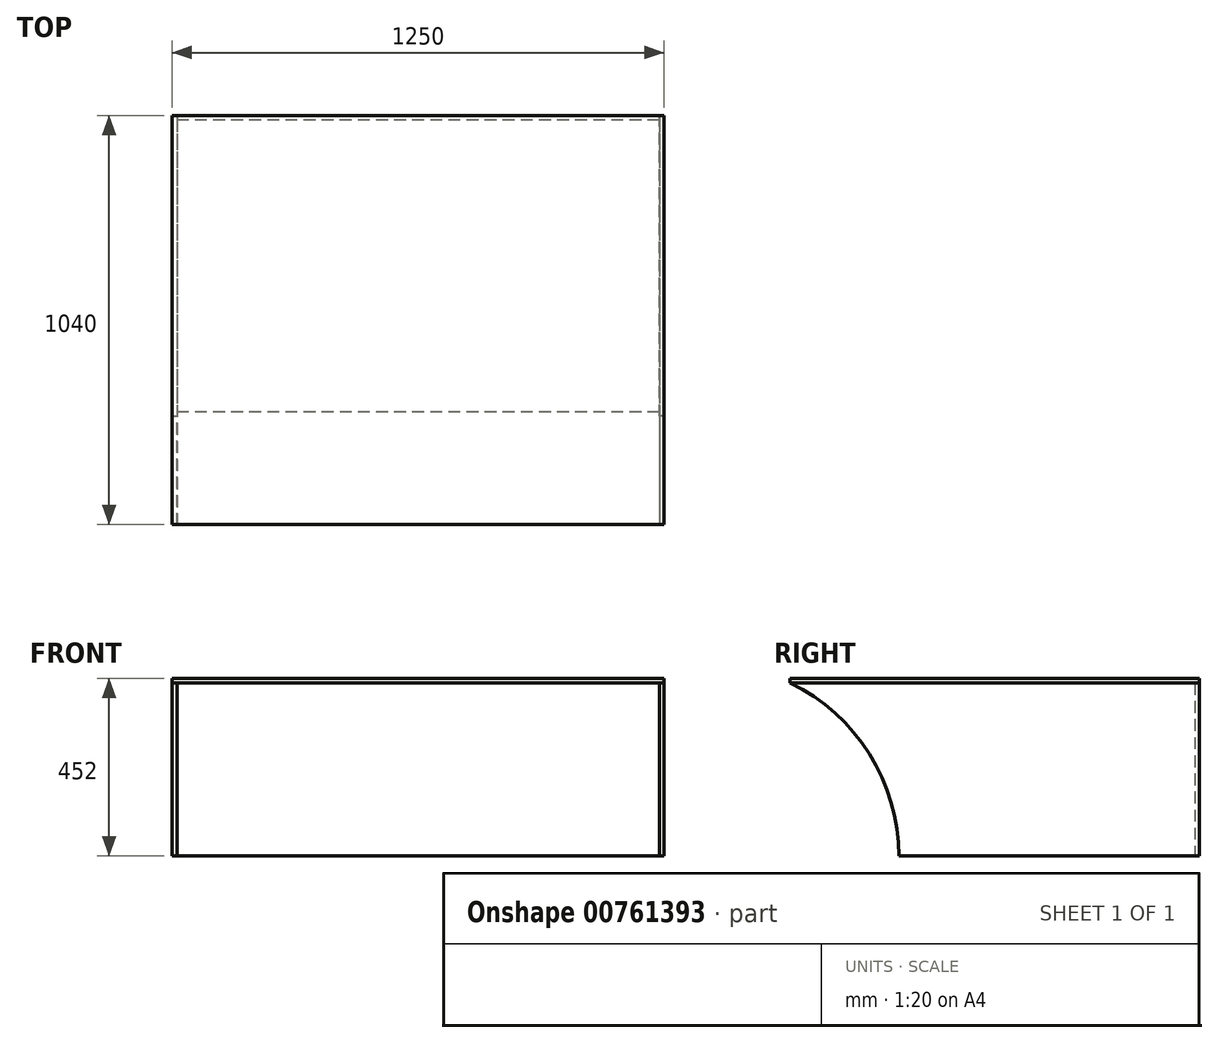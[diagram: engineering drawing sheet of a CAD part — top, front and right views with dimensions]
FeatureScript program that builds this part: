
annotation { "Feature Type Name" : "Feature", "Feature Type Description" : "" }
export const myFeature = defineFeature(function(context is Context, id is Id, definition is map)
    precondition{}
    {
        {
            var Q0;
            Q0=qCreatedBy(makeId("Top.planeOp"),FACE);
            var sketch = newSketch(context, id + "F0", { "sketchPlane" : qUnion([Q0])});
            skLineSegment(sketch, "E0.bottom", {"start": v(-622.3, 286.42) * mm, "end": v(603.7, 286.42) * mm});
            skLineSegment(sketch, "E0.top", {"start": v(-622.3, -453.58) * mm, "end": v(603.7, -453.58) * mm});
            skLineSegment(sketch, "E0.left", {"start": v(-622.3, 286.42) * mm, "end": v(-622.3, -453.58) * mm});
            skLineSegment(sketch, "E0.right", {"start": v(603.7, 286.42) * mm, "end": v(603.7, -453.58) * mm});
            skSolve(sketch);
        }
        {
            var Q0;
            Q0=makeQuery(id+"F0.imprint","IMPRINT",FACE,{"disambiguationData":[TD([[makeQuery(id+"F0.imprint","IMPRINT",EDGE,{"derivedFrom":sQuery(id+"F0.wireOp",EDGE,"E0.bottom")}),-1.0]])]});
            extrude(context, id + "F1", {"entities" : qUnion([Q0]), "depth" : 1 * mm, "offsetDistance" : 25 * mm});
        }
        {
            var Q0;
            Q0=makeQuery(id+"F1.opExtrude","SWEPT_FACE",FACE,{"disambiguationData":[OSD([sQuery(id+"F0.wireOp",EDGE,"E0.bottom")])]});
            var sketch = newSketch(context, id + "F2", { "sketchPlane" : qUnion([Q0])});
            skLineSegment(sketch, "E1.bottom", {"start": v(-603.7, 440) * mm, "end": v(622.3, 440) * mm});
            skLineSegment(sketch, "E1.top", {"start": v(-603.7, 0) * mm, "end": v(622.3, 0) * mm});
            skLineSegment(sketch, "E1.left", {"start": v(-603.7, 440) * mm, "end": v(-603.7, 0) * mm});
            skLineSegment(sketch, "E1.right", {"start": v(622.3, 440) * mm, "end": v(622.3, 0) * mm});
            skSolve(sketch);
        }
        {
            var Q0;
            {var subQ0=sQuery(id+"F2.wireOp",EDGE,"E1.bottom");Q0=makeQuery(id+"F2.imprint","IMPRINT",FACE,{"disambiguationData":[TD([[makeQuery(id+"F2.imprint","IMPRINT",EDGE,{"derivedFrom":subQ0}),-1.0]])]});}
            var Q1;
            {var subQ0=sQuery(id+"F2.wireOp",EDGE,"E1.top");Q1=makeQuery(id+"F2.imprint","IMPRINT",FACE,{"disambiguationData":[TD([[makeQuery(id+"F2.imprint","IMPRINT",EDGE,{"derivedFrom":subQ0}),-1.0]])]});}
            extrude(context, id + "F3", {"entities" : qUnion([Q0, Q1]), "depth" : 12 * mm, "offsetDistance" : 25 * mm});
        }
        {
            var Q0;
            Q0=makeQuery(id+"F1.opExtrude","SWEPT_FACE",FACE,{"disambiguationData":[OSD([sQuery(id+"F0.wireOp",EDGE,"E0.top")])]});
            var sketch = newSketch(context, id + "F4", { "sketchPlane" : qUnion([Q0])});
            skLineSegment(sketch, "E2.bottom", {"start": v(-622.3, 440) * mm, "end": v(603.7, 440) * mm});
            skLineSegment(sketch, "E2.top", {"start": v(-622.3, 0) * mm, "end": v(603.7, 0) * mm});
            skLineSegment(sketch, "E2.left", {"start": v(-622.3, 440) * mm, "end": v(-622.3, 0) * mm});
            skLineSegment(sketch, "E2.right", {"start": v(603.7, 440) * mm, "end": v(603.7, 0) * mm});
            skSolve(sketch);
        }
        {
            var Q0;
            Q0=makeQuery(id+"F3.opExtrude","SWEPT_FACE",FACE,{"disambiguationData":[OSD([sQuery(id+"F2.wireOp",EDGE,"E1.right")])]});
            var sketch = newSketch(context, id + "F5", { "sketchPlane" : qUnion([Q0])});
            skLineSegment(sketch, "E3.bottom", {"start": v(-298.42, 440) * mm, "end": v(741.58, 440) * mm});
            skLineSegment(sketch, "E3.top", {"start": v(-298.42, 0) * mm, "end": v(465.58, 0) * mm});
            skLineSegment(sketch, "E3.left", {"start": v(-298.42, 440) * mm, "end": v(-298.42, 0) * mm});
            skArc(sketch, "E4", {"start": v(741.58, 440) * mm, "mid": v(540.3, 259.7) * mm, "end": v(465.58, 0) * mm});
            skSolve(sketch);
        }
        {
            var Q0;
            {var subQ2=sQuery(id+"F5.wireOp",EDGE,"E4");Q0=makeQuery(id+"F5.imprint","IMPRINT",FACE,{"disambiguationData":[TD([[makeQuery(id+"F5.imprint","IMPRINT",EDGE,{"derivedFrom":subQ2}),-1.0]])]});}
            var Q1;
            {var subQ2=sQuery(id+"F5.wireOp",EDGE,"E3.left");Q1=makeQuery(id+"F5.imprint","IMPRINT",FACE,{"disambiguationData":[TD([[makeQuery(id+"F5.imprint","IMPRINT",EDGE,{"derivedFrom":subQ2}),1.0]])]});}
            extrude(context, id + "F6", {"entities" : qUnion([Q0, Q1]), "depth" : 12 * mm, "offsetDistance" : 25 * mm});
        }
        {
            var Q0;
            Q0=makeQuery(id+"F3.opExtrude","SWEPT_FACE",FACE,{"disambiguationData":[OSD([sQuery(id+"F2.wireOp",EDGE,"E1.left")])]});
            var sketch = newSketch(context, id + "F7", { "sketchPlane" : qUnion([Q0])});
            skLineSegment(sketch, "E5", {"start": v(-465.58, 0) * mm, "end": v(298.42, 0) * mm});
            skLineSegment(sketch, "E6", {"start": v(298.42, 0) * mm, "end": v(298.42, 440) * mm});
            skLineSegment(sketch, "E7", {"start": v(298.42, 440) * mm, "end": v(-741.58, 440) * mm});
            skArc(sketch, "E8", {"start": v(-465.58, 0) * mm, "mid": v(-540.3, 259.7) * mm, "end": v(-741.58, 440) * mm});
            skSolve(sketch);
        }
        {
            var Q0;
            Q0 = qSketchRegion(id + "F7", true);
            extrude(context, id + "F8", {"entities" : qUnion([Q0]), "depth" : 12 * mm, "offsetDistance" : 25 * mm});
        }
        {
            var Q0;
            Q0=makeQuery(id+"F3.opExtrude","SWEPT_FACE",FACE,{"disambiguationData":[OSD([sQuery(id+"F2.wireOp",EDGE,"E1.bottom")])]});
            var sketch = newSketch(context, id + "F9", { "sketchPlane" : qUnion([Q0])});
            skLineSegment(sketch, "E9.bottom", {"start": v(-634.3, 298.42) * mm, "end": v(615.7, 298.42) * mm});
            skLineSegment(sketch, "E9.top", {"start": v(-634.3, -741.58) * mm, "end": v(615.7, -741.58) * mm});
            skLineSegment(sketch, "E9.left", {"start": v(-634.3, 298.42) * mm, "end": v(-634.3, -741.58) * mm});
            skLineSegment(sketch, "E9.right", {"start": v(615.7, 298.42) * mm, "end": v(615.7, -741.58) * mm});
            skSolve(sketch);
        }
        {
            var Q0;
            Q0 = qSketchRegion(id + "F9", true);
            extrude(context, id + "F10", {"entities" : qUnion([Q0]), "depth" : 12 * mm, "offsetDistance" : 25 * mm});
        }
    });
